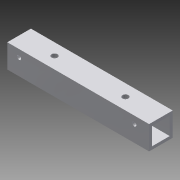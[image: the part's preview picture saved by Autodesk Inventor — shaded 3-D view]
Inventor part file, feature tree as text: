
AUTODESK INVENTOR PART (.ipt)
format: ipt  version: 2015 SP1 (Build 190203100, 203)  size: 118,784 bytes
history: native  units: in
note: dims shown in document units (in); Inventor stores cm internally (conversion verified against a paired STEP export)
features: sketch x3, hole x2, extrude x1
ambient origin geometry x8: Origin, YZ Plane, XZ Plane, XY Plane, X Axis, Y Axis, Z Axis, Center Point
bodies: Solid1 (feature_tree)
feature tree (6):
  extrude  "Extrusion1"  Depth=1.0in
  hole  "Hole1"  [1 undecoded]
  hole  "Hole2"  [1 undecoded]
  sketch  "Sketch1"  dims[d0=1.0in d1=1.0in]
  sketch  "Sketch2"  dims[d2=0.75in d3=0.75in]
  sketch  "Sketch3"  dims[d4=0.125in d5=0.125in d6=6.0in d7=0.0in d8=1.5in d9=0.5in d10=0.5in d11=1.5in d12=0.25in d13=0.75in d14=0.375in d15=0.25in d16=0.5635in d17=1.0in d18=0.8108in d19=0.625in d20=0.6875in d21=0.5in d22=0.6875in d23=0.1719in d24=0.75in d25=0.375in d26=0.25in d27=0.5635in d28=1.0in d29=0.8108in]
note: 2 required parameter values undecoded (feature->parameter linkage not recoverable at this tier; creation-order binding heuristic only, values carry confidence <= 0.55)
